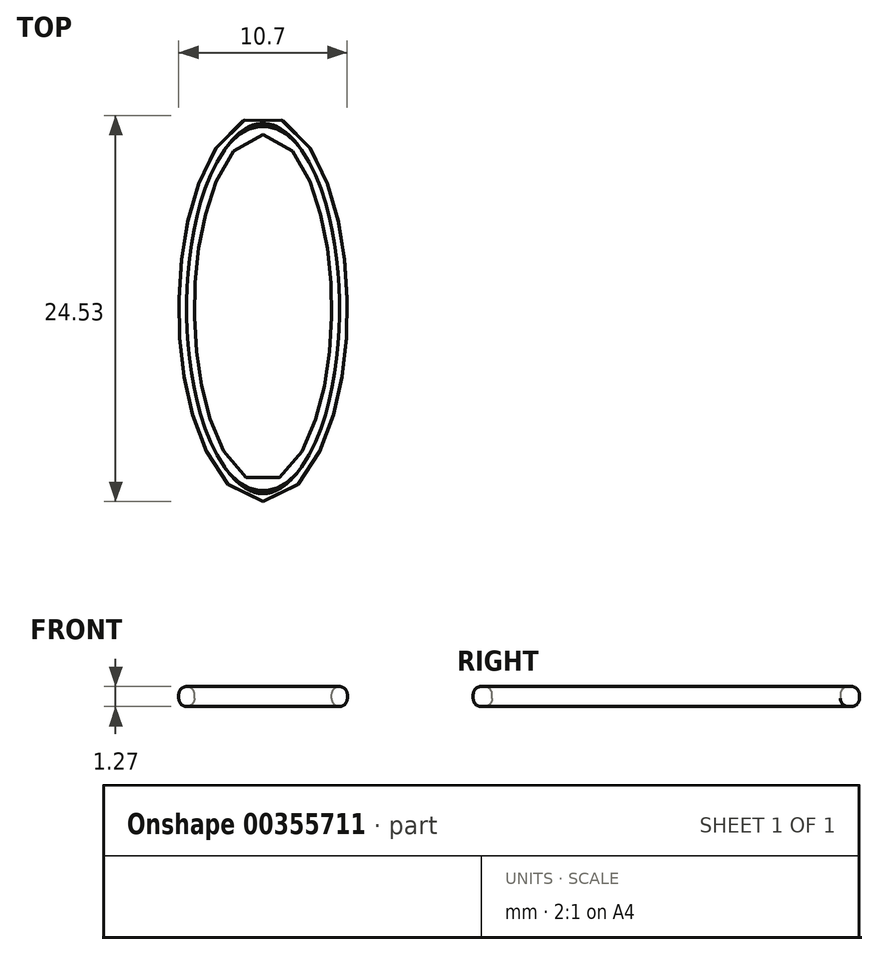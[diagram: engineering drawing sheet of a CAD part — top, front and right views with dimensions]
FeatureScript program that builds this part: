
annotation { "Feature Type Name" : "Feature", "Feature Type Description" : "" }
export const myFeature = defineFeature(function(context is Context, id is Id, definition is map)
    precondition{}
    {
        {
            var Q0;
            Q0=qCreatedBy(makeId("Top.planeOp"),FACE);
            var sketch = newSketch(context, id + "F0", { "sketchPlane" : qUnion([Q0])});
            skEllipse(sketch, "E0", {"center": v(-43.25, 28.4) * mm, "majorRadius": 12.26 * mm, "minorRadius": 5.35 * mm, "majorAxis": v(0, -1)});
            skEllipse(sketch, "E1", {"center": v(-43.25, 28.4) * mm, "majorRadius": 11.06 * mm, "minorRadius": 4.35 * mm, "majorAxis": v(0, 1)});
            skSolve(sketch);
        }
        {
            var Q0;
            Q0=makeQuery(id+"F0.imprint","IMPRINT",FACE,{"disambiguationData":[TD([[makeQuery(id+"F0.imprint","IMPRINT",EDGE,{"derivedFrom":sQuery(id+"F0.wireOp",EDGE,"E0")}),1.0]])]});
            extrude(context, id + "F1", {"entities" : qUnion([Q0]), "depth" : 1.27 * mm});
        }
        {
            var Q0;
            Q0=makeQuery(id+"F1.opExtrude","CAP_EDGE",EDGE,{"disambiguationData":[OSD([sQuery(id+"F0.wireOp",EDGE,"E0")])],"isStart":true});
            var Q1;
            Q1=makeQuery(id+"F1.opExtrude","CAP_EDGE",EDGE,{"disambiguationData":[OSD([sQuery(id+"F0.wireOp",EDGE,"E0")])],"isStart":false});
            var Q2;
            Q2=makeQuery(id+"F1.opExtrude","CAP_FACE",FACE,{"disambiguationData":[OSD([sQuery(id+"F0.wireOp",EDGE,"E0"),sQuery(id+"F0.wireOp",EDGE,"E1")])],"isStart":false});
            var Q3;
            Q3=makeQuery(id+"F1.opExtrude","SWEPT_FACE",FACE,{"disambiguationData":[OSD([sQuery(id+"F0.wireOp",EDGE,"E0")])]});
            var Q4;
            Q4=makeQuery(id+"F1.opExtrude","CAP_FACE",FACE,{"disambiguationData":[OSD([sQuery(id+"F0.wireOp",EDGE,"E0"),sQuery(id+"F0.wireOp",EDGE,"E1")])],"isStart":true});
            var Q5;
            Q5=makeQuery(id+"F1.opExtrude","CAP_EDGE",EDGE,{"disambiguationData":[OSD([sQuery(id+"F0.wireOp",EDGE,"E1")])],"isStart":false});
            var Q6;
            Q6=makeQuery(id+"F1.opExtrude","SWEPT_FACE",FACE,{"disambiguationData":[OSD([sQuery(id+"F0.wireOp",EDGE,"E1")])]});
            var Q7;
            Q7=makeQuery(id+"F1.opExtrude","CAP_EDGE",EDGE,{"disambiguationData":[OSD([sQuery(id+"F0.wireOp",EDGE,"E1")])],"isStart":true});
            fillet(context, id + "F2", {"entities" : qUnion([Q0, Q1, Q2, Q3, Q4, Q5, Q6, Q7]), "radius" : 0.5 * mm, "tangentPropagation" : true, "allowEdgeOverflow" : false});
        }
    });
